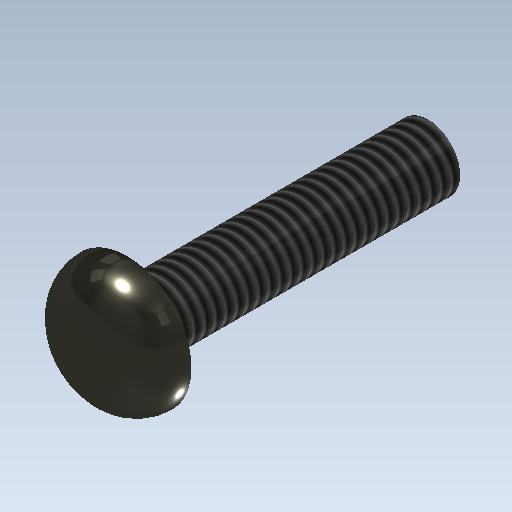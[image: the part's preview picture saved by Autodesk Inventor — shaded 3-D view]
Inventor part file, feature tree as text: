
AUTODESK INVENTOR PART (.ipt)
format: ipt  version: 2020.2 (Build 242310000, 310)  size: 182,272 bytes
history: native  units: mm
features: extrude x5, sketch x5, other x1, fillet x1, thread x1
ambient origin geometry x1: Origin
bodies: Body1 (feature_tree)
feature tree (13):
  other  "ソリッド1"
  extrude  "押し出し1"  Depth=3.0mm
  extrude  "押し出し2"  Depth=6.0mm TaperAngle=0.0deg
  fillet  "フィレット1"  Radius=6.0mm
  thread  "ねじ1"
  extrude  "押し出し3"  Depth=2.0mm TaperAngle=0.0deg
  extrude  "押し出し4"  Depth=2.0mm
  extrude  "押し出し5"  Depth=10.0mm TaperAngle=0.0deg
  sketch  "スケッチ1"
  sketch  "スケッチ2"
  sketch  "スケッチ3"
  sketch  "スケッチ4"
  sketch  "スケッチ5"
